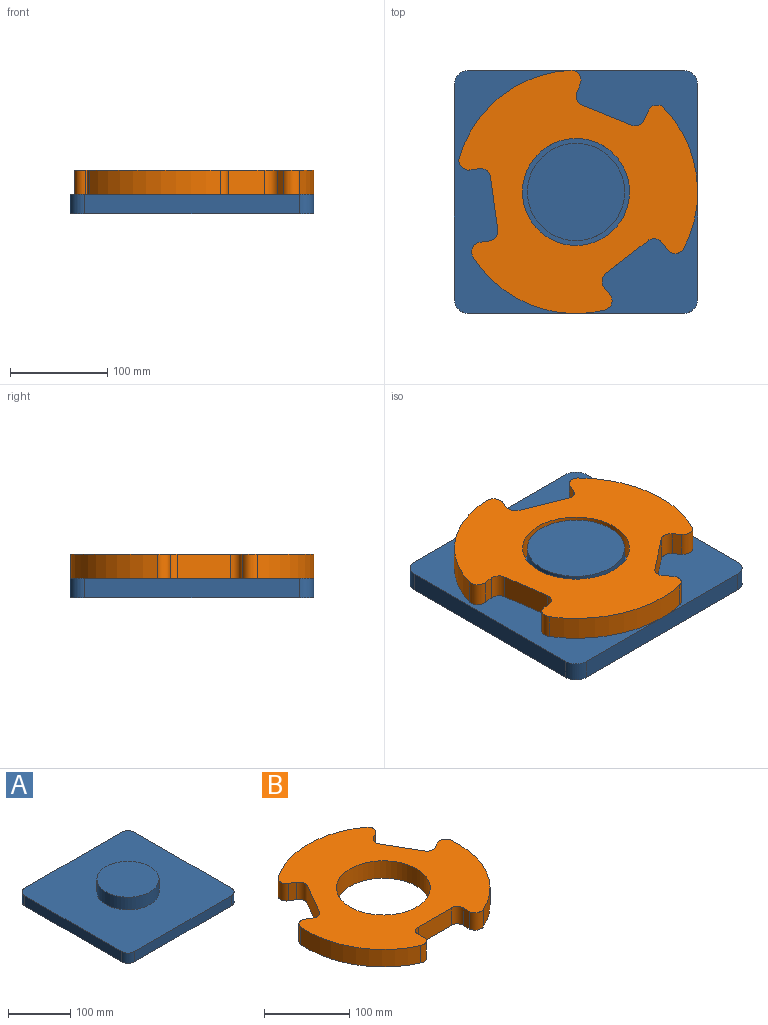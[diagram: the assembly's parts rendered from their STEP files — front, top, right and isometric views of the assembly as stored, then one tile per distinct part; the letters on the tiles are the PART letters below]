
ASSEMBLY  parts=2 mates=1
PART A: 12 faces, bbox 250x250x45 mm
  f0: plane 220x20mm, normal (1,0,0), area 4400mm2, adj f4,f5,f8,f11
  f1: plane 220x20mm, normal (0,1,0), area 4400mm2, adj f4,f5,f8,f9
  f2: plane 220x20mm, normal (-1,0,0), area 4400mm2, adj f4,f5,f9,f10
  f3: plane 220x20mm, normal (0,-1,0), area 4400mm2, adj f4,f5,f10,f11
  f4: plane 250x250mm, normal (0,0,1), area 54452.9mm2, adj f0,f1,f2,f3,f6,f8,f9,f10
  f5: plane 250x250mm, normal (0,0,-1), area 62306.9mm2, adj f0,f1,f2,f3,f8,f9,f10,f11
  f6: cylinder r=50mm len=100mm, axis (0,0,-1), area 7854mm2, adj f4,f7
  f7: plane 100x100mm, normal (0,0,1), area 7854mm2, adj f6
  f8: cylinder r=15mm len=20mm, axis (0,0,-1), area 471.2mm2, adj f0,f1,f4,f5
  f9: cylinder r=15mm len=20mm, axis (0,0,1), area 471.2mm2, adj f1,f2,f4,f5
  f10: cylinder r=15mm len=20mm, axis (0,0,-1), area 471.2mm2, adj f2,f3,f4,f5
  f11: cylinder r=15mm len=20mm, axis (0,0,1), area 471.2mm2, adj f0,f3,f4,f5
PART B: 27 faces, bbox 250x239.7x25 mm
  f0: plane 250x239.73mm, normal (0,0,1), area 30837.4mm2, adj f2,f3,f4,f5,f6,f7,f8,f9
  f1: plane 250x239.73mm, normal (0,0,-1), area 30837.4mm2, adj f2,f3,f4,f5,f6,f7,f8,f9
  f2: cylinder r=125mm len=145.54mm, axis (0,0,-1), area 3883.8mm2, adj f0,f1,f18,f26
  f3: cylinder r=125mm len=126.05mm, axis (0,0,-1), area 3883.8mm2, adj f0,f1,f11,f19
  f4: cylinder r=55mm len=110mm, axis (0,0,-1), area 8639.4mm2, adj f0,f1
  f5: cylinder r=125mm len=126.05mm, axis (0,0,-1), area 3883.8mm2, adj f0,f1,f12,f25
  f6: plane 25x9.73mm, normal (-1,0,0), area 243.3mm2, adj f0,f1,f9,f12
  f7: plane 55x25mm, normal (0,-1,0), area 1375mm2, adj f0,f1,f9,f10
  f8: plane 25x9.73mm, normal (1,0,0), area 243.3mm2, adj f0,f1,f10,f11
  f9: cylinder r=10mm len=25mm, axis (0,0,-1), area 392.7mm2, adj f0,f1,f6,f7
  f10: cylinder r=10mm len=25mm, axis (0,0,-1), area 392.7mm2, adj f0,f1,f7,f8
  f11: cylinder r=10mm len=25mm, axis (0,0,-1), area 499.1mm2, adj f0,f1,f3,f8
  f12: cylinder r=10mm len=25mm, axis (0,0,-1), area 499.1mm2, adj f0,f1,f5,f6
  f13: plane 25x8.43mm, normal (0.5,0.87,0), area 243.3mm2, adj f0,f1,f16,f19
  f14: plane 47.63x27.5mm, normal (-0.87,0.5,0), area 1375mm2, adj f0,f1,f16,f17
  f15: plane 25x8.43mm, normal (-0.5,-0.87,0), area 243.3mm2, adj f0,f1,f17,f18
  f16: cylinder r=10mm len=25mm, axis (0,0,-1), area 392.7mm2, adj f0,f1,f13,f14
  f17: cylinder r=10mm len=25mm, axis (0,0,-1), area 392.7mm2, adj f0,f1,f14,f15
  f18: cylinder r=10mm len=25mm, axis (0,0,-1), area 499.1mm2, adj f0,f1,f2,f15
  f19: cylinder r=10mm len=25mm, axis (0,0,-1), area 499.1mm2, adj f0,f1,f3,f13
  f20: plane 25x8.43mm, normal (0.5,-0.87,0), area 243.3mm2, adj f0,f1,f23,f26
  f21: plane 47.63x27.5mm, normal (0.87,0.5,0), area 1375mm2, adj f0,f1,f23,f24
  f22: plane 25x8.43mm, normal (-0.5,0.87,0), area 243.3mm2, adj f0,f1,f24,f25
  f23: cylinder r=10mm len=25mm, axis (0,0,-1), area 392.7mm2, adj f0,f1,f20,f21
  f24: cylinder r=10mm len=25mm, axis (0,0,-1), area 392.7mm2, adj f0,f1,f21,f22
  f25: cylinder r=10mm len=25mm, axis (0,0,-1), area 499.1mm2, adj f0,f1,f5,f22
  f26: cylinder r=10mm len=25mm, axis (0,0,-1), area 499.1mm2, adj f0,f1,f2,f20
PLACE A at identity fixed
PLACE B rot(axis=(0,0,1),158deg) t=(0,0,0)mm
MATE revolute A.f6 <-> B.f2  axis (0,0,1) through (0,0,45)mm
